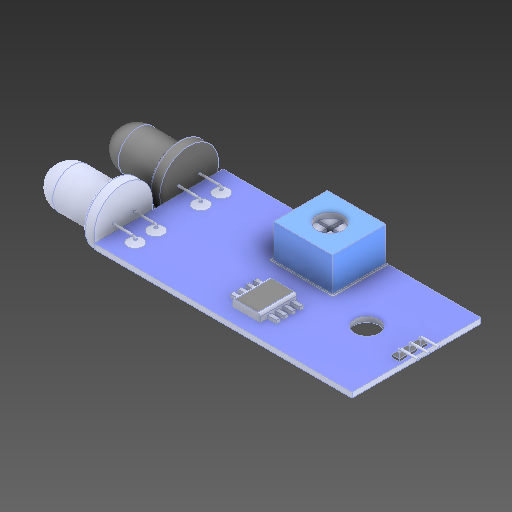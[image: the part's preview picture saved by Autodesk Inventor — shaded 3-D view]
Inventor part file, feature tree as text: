
AUTODESK INVENTOR PART (.ipt)
format: ipt  version: 2020.2 (Build 242310000, 310)  size: 313,344 bytes
history: mixed  units: mm
features: fillet x1, imported_body x1
ambient origin geometry x8: Origin, YZ Plane, XZ Plane, XY Plane, X Axis, Y Axis, Z Axis, Center Point
bodies: Solid1 (imported_parasolid)
feature tree (2):
  fillet  "Fillet3"  [1 undecoded]
  imported_body  NMx_Import_Brep_tag  [imported B-rep: ~6 faces, bbox_mm=None]
note: 1 required parameter value undecoded (feature->parameter linkage not recoverable at this tier; creation-order binding heuristic only, values carry confidence <= 0.55)
